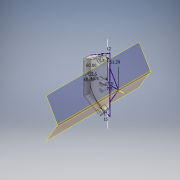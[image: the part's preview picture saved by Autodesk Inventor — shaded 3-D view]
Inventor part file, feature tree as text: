
AUTODESK INVENTOR PART (.ipt)
format: ipt  version: 2019.3 (Build 233278000, 278)  size: 231,424 bytes
history: native  units: mm
features: sketch x7, sweep x3, plane x2, chamfer x2, extrude x1, hole x1, shell x1
ambient origin geometry x8: Origin, YZ Plane, XZ Plane, XY Plane, X Axis, Y Axis, Z Axis, Center Point
bodies: Solid1 (feature_tree)
feature tree (17):
  extrude  "Extrusion1"  Depth=7.5mm
  sketch  "Sketch3"  dims[d3=51.29mm d11=7.5mm]
  sketch  "Sketch4"  dims[d12=7.5mm d13=12.5mm]
  plane  "Work Plane1"
  plane  "Work Plane2"
  sketch  "Sketch5"  dims[d14=12.5mm d15=30.0mm d16=0.0mm]
  sweep  "Sweep1"
  sweep  "Sweep2"
  sweep  "Sweep3"
  chamfer  "Chamfer1"  Distance=5.0mm
  chamfer  "Chamfer2"  [1 undecoded]
  hole  "Hole1"  [1 undecoded]
  shell  "Shell1"  Thickness=14.424978mm
  sketch  "Sketch6"  dims[d21=60.0deg d22=60.0deg]
  sketch  "Sketch7"  dims[d23=5.1mm]
  sketch  "Sketch8"  dims[d24=10.2mm]
  sketch  "Sketch10"  dims[d25=14.424978mm d26=5.0mm d29=0.0mm d30=0.0mm d31=5.1mm d32=14.424978mm d33=10.2mm d34=5.0mm d35=0.0mm d36=0.0mm d37=5.1mm d38=10.2mm d39=14.424978mm d40=5.0mm d41=0.0mm d42=0.0mm d44=12.0mm d45=15.0mm d46=40.0mm d47=2.0mm d48=30.0deg d49=40.0mm d50=2.0mm d51=30.0deg d53=10.0mm d54=10.0mm d55=10.0mm d56=7.5mm d57=6.0mm d58=13.5mm d59=5.0mm d60=90.0deg d61=20.0mm d62=20.594885mm d63=4.0mm]
note: 2 required parameter values undecoded (feature->parameter linkage not recoverable at this tier; creation-order binding heuristic only, values carry confidence <= 0.55)
